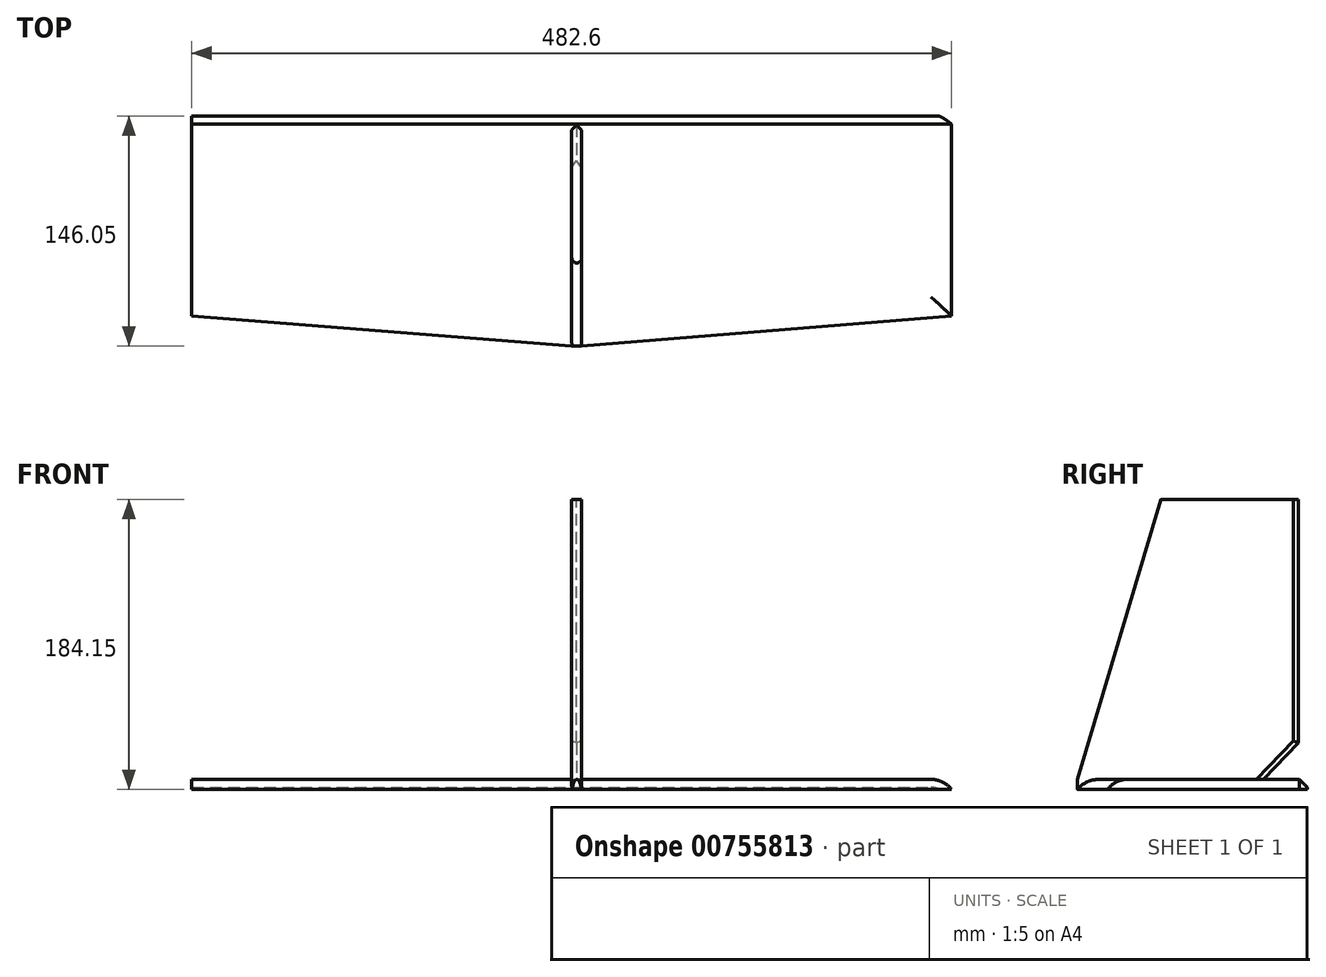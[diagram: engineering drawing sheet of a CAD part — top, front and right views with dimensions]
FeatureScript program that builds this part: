
annotation { "Feature Type Name" : "Feature", "Feature Type Description" : "" }
export const myFeature = defineFeature(function(context is Context, id is Id, definition is map)
    precondition{}
    {
        {
            var Q0;
            Q0=qCreatedBy(makeId("Right.planeOp"),FACE);
            var sketch = newSketch(context, id + "F0", { "sketchPlane" : qUnion([Q0])});
            skLineSegment(sketch, "E0.bottom", {"start": v(0, 85.16) * mm, "end": v(89.45, 85.16) * mm});
            skLineSegment(sketch, "E0.top", {"start": v(-52.8, -92.64) * mm, "end": v(67.7, -92.64) * mm});
            skLineSegment(sketch, "E0.right", {"start": v(89.45, 85.16) * mm, "end": v(89.45, -70.22) * mm});
            skLineSegment(sketch, "E1", {"start": v(-52.8, -92.64) * mm, "end": v(0, 85.16) * mm});
            skLineSegment(sketch, "E2", {"start": v(89.45, -70.22) * mm, "end": v(67.7, -92.64) * mm});
            skSolve(sketch);
        }
        {
            var Q0;
            Q0=makeQuery(id+"F0.imprint","IMPRINT",FACE,{"disambiguationData":[TD([[makeQuery(id+"F0.imprint","IMPRINT",EDGE,{"derivedFrom":sQuery(id+"F0.wireOp",EDGE,"E0.bottom")}),-1.0]])]});
            extrude(context, id + "F1", {"entities" : qUnion([Q0]), "depth" : 6.35 * mm, "offsetDistance" : 25.4 * mm});
        }
        {
            var Q0;
            Q0=makeQuery(id+"F1.opExtrude","SWEPT_FACE",FACE,{"disambiguationData":[OSD([sQuery(id+"F0.wireOp",EDGE,"E0.top")])]});
            var sketch = newSketch(context, id + "F2", { "sketchPlane" : qUnion([Q0])});
            skLineSegment(sketch, "E3.bottom", {"start": v(0, 52.8) * mm, "end": v(6.35, 52.8) * mm});
            skLineSegment(sketch, "E3.top", {"start": v(-241.3, -93.26) * mm, "end": v(241.3, -93.26) * mm});
            skLineSegment(sketch, "E3.left", {"start": v(-241.3, 33.74) * mm, "end": v(-241.3, -93.26) * mm});
            skLineSegment(sketch, "E3.right", {"start": v(241.3, 33.74) * mm, "end": v(241.3, -93.26) * mm});
            skLineSegment(sketch, "E4", {"start": v(0, 52.8) * mm, "end": v(-241.3, 33.74) * mm});
            skLineSegment(sketch, "E5", {"start": v(6.35, 52.8) * mm, "end": v(241.3, 33.74) * mm});
            skPoint(sketch, "E6.orphan", {"position": v(-241.3, 52.8) * mm});
            skPoint(sketch, "E7.center.orphan", {"position": v(241.37, 14.7) * mm});
            skPoint(sketch, "E8.center.orphan", {"position": v(-222.25, 14.7) * mm});
            skSolve(sketch);
        }
        {
            var Q0;
            Q0=qSketchRegion(id+"F2",true);
            extrude(context, id + "F3", {"entities" : qUnion([Q0]), "operationType" : NewBodyOperationType.ADD, "depth" : 6.35 * mm, "offsetDistance" : 25.4 * mm});
        }
        {
            var Q0;
            Q0=makeQuery(id+"F1.opExtrude","CAP_EDGE",EDGE,{"disambiguationData":[OSD([sQuery(id+"F0.wireOp",EDGE,"E1")])],"isStart":false});
            var Q1;
            Q1=makeQuery(id+"F1.opExtrude","CAP_EDGE",EDGE,{"disambiguationData":[OSD([sQuery(id+"F0.wireOp",EDGE,"E1")])],"isStart":true});
            fillet(context, id + "F4", {"entities" : qUnion([Q0, Q1]), "radius" : 3.07 * mm, "tangentPropagation" : true, "allowEdgeOverflow" : false});
        }
        {
            var Q0;
            Q0=makeQuery(id+"F3.opExtrude","CAP_EDGE",EDGE,{"disambiguationData":[OSD([sQuery(id+"F2.wireOp",EDGE,"E5")])],"isStart":true});
            var Q1;
            Q1=makeQuery(id+"F3.opExtrude","CAP_EDGE",EDGE,{"disambiguationData":[OSD([sQuery(id+"F2.wireOp",EDGE,"E4")])],"isStart":true});
            var Q2;
            Q2=makeQuery(id+"F3.opExtrude","CAP_EDGE",EDGE,{"disambiguationData":[OSD([sQuery(id+"F2.wireOp",EDGE,"E7")])],"isStart":true});
            var Q3;
            Q3=makeQuery(id+"F3.opExtrude","CAP_EDGE",EDGE,{"disambiguationData":[OSD([sQuery(id+"F2.wireOp",EDGE,"E3.right")])],"isStart":true});
            fillet(context, id + "F5", {"entities" : qUnion([Q0, Q1, Q2, Q3]), "radius" : 16.56 * mm, "tangentPropagation" : true, "allowEdgeOverflow" : false});
        }
        {
            var Q0;
            Q0=makeQuery(id+"F1.opExtrude","CAP_EDGE",EDGE,{"disambiguationData":[OSD([sQuery(id+"F0.wireOp",EDGE,"E0.right")])],"isStart":true});
            var Q1;
            Q1=makeQuery(id+"F1.opExtrude","CAP_EDGE",EDGE,{"disambiguationData":[OSD([sQuery(id+"F0.wireOp",EDGE,"E0.right")])],"isStart":false});
            chamfer(context, id + "F6", {"entities" : qUnion([Q0, Q1]), "width" : 5.08 * mm, "tangentPropagation" : true});
        }
        {
            var Q0;
            Q0=makeQuery(id+"F1.opExtrude","CAP_EDGE",EDGE,{"disambiguationData":[OSD([sQuery(id+"F0.wireOp",EDGE,"E2")])],"isStart":false});
            var Q1;
            Q1=makeQuery(id+"F1.opExtrude","CAP_EDGE",EDGE,{"disambiguationData":[OSD([sQuery(id+"F0.wireOp",EDGE,"E2")])],"isStart":true});
            chamfer(context, id + "F7", {"entities" : qUnion([Q0, Q1]), "width" : 5.08 * mm, "tangentPropagation" : true});
        }
        {
            var Q0;
            Q0=makeQuery(id+"F3.opExtrude","CAP_EDGE",EDGE,{"disambiguationData":[OSD([sQuery(id+"F2.wireOp",EDGE,"E3.top")])],"isStart":true});
            chamfer(context, id + "F8", {"entities" : qUnion([Q0]), "width" : 5.08 * mm, "tangentPropagation" : true});
        }
    });
